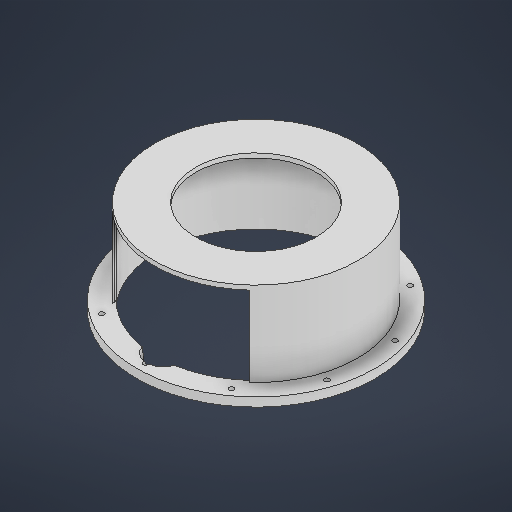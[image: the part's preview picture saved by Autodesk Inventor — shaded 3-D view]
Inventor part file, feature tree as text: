
AUTODESK INVENTOR PART (.ipt)
format: ipt  version: 2025 (Build 290162000, 162)  size: 296,960 bytes
history: native  units: in
note: dims shown in document units (in); Inventor stores cm internally (conversion verified against a paired STEP export)
features: sketch x6, extrude x5, plane x3, fillet x1
ambient origin geometry x8: Origin, YZ Plane, XZ Plane, XY Plane, X Axis, Y Axis, Z Axis, Center Point
bodies: Solid1 (feature_tree)
feature tree (15):
  sketch  "Sketch1"  dims[d5=0.0in d7=0.0in]
  extrude  "Extrusion1"  TaperAngle=0.0deg  [1 undecoded]
  extrude  "Extrusion2"  Depth=4.5276in
  extrude  "Extrusion7"  Depth=0.2165in
  extrude  "Extrusion34"  Depth=6.1024in
  sketch  "Sketch30"  dims[d272=3.937in d273=4.1535in d274=0.0in d285=3.937in]
  plane  "Work Plane19"
  plane  "Work Plane21"
  plane  "Work Plane22"
  extrude  "Extrusion36"  Depth=4.1535in TaperAngle=0.0deg
  fillet  "Fillet19"  Radius=3.937in
  sketch  "Sketch2"  dims[d18=0.0in d52=4.5276in]
  sketch  "Sketch Circular Pattern5"  dims[d264=9.8425in d265=0.2165in]
  sketch  "Sketch28"  dims[d266=3.937in d268=360.0deg d271=6.1024in]
  sketch  "Sketch31"  dims[d286=1.5748in d287=2.0812in d288=0.0in d289=3.5039in d290=0.1969in d113=0.0197in d114=0.0344in d115=0.0197in d116=0.0344in d167=0.0197in d168=0.0344in d169=0.0197in d170=0.0344in d215=0.0197in d216=0.0344in d217=0.0197in d218=0.0344in d219=0.0in d220=0.0in d254=0.0197in d255=0.0344in d256=0.0197in d257=0.0344in]
note: 1 required parameter value undecoded (feature->parameter linkage not recoverable at this tier; creation-order binding heuristic only, values carry confidence <= 0.55)
